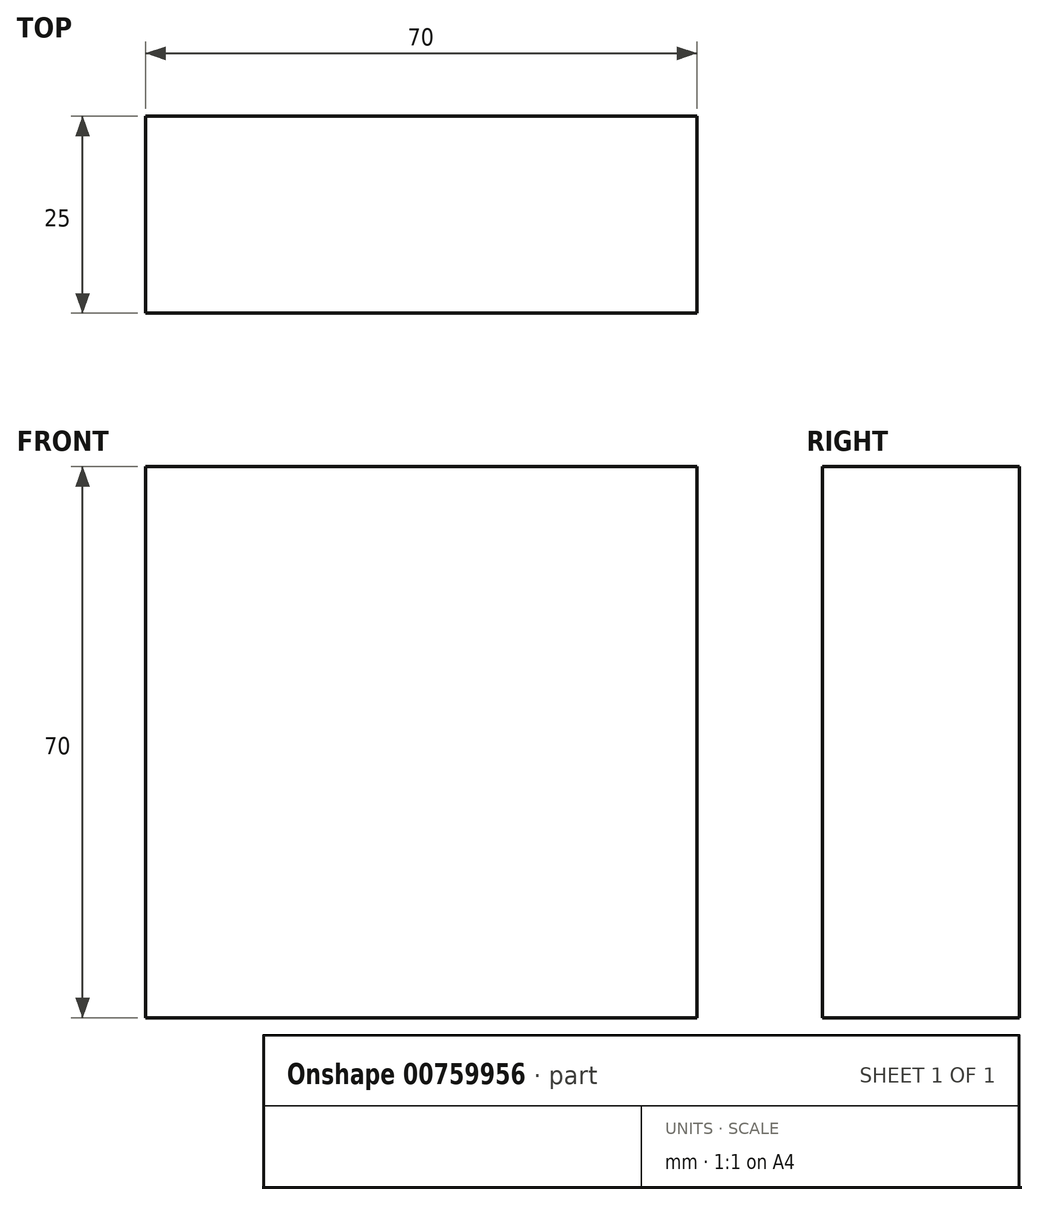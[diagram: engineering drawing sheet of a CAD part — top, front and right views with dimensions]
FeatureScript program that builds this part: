
annotation { "Feature Type Name" : "Feature", "Feature Type Description" : "" }
export const myFeature = defineFeature(function(context is Context, id is Id, definition is map)
    precondition{}
    {
        {
            var Q0;
            Q0=qCreatedBy(makeId("Front.planeOp"),FACE);
            var sketch = newSketch(context, id + "F0", { "sketchPlane" : qUnion([Q0])});
            skLineSegment(sketch, "E0.bottom", {"start": v(-35, 35) * mm, "end": v(35, 35) * mm});
            skLineSegment(sketch, "E0.top", {"start": v(-35, -35) * mm, "end": v(35, -35) * mm});
            skLineSegment(sketch, "E0.left", {"start": v(-35, 35) * mm, "end": v(-35, -35) * mm});
            skLineSegment(sketch, "E0.right", {"start": v(35, 35) * mm, "end": v(35, -35) * mm});
            skPoint(sketch, "E0.middle", {"position": v(0, 0) * mm});
            skSolve(sketch);
        }
        {
            var Q0;
            Q0=makeQuery(id+"F0.imprint","IMPRINT",FACE,{"disambiguationData":[TD([[makeQuery(id+"F0.imprint","IMPRINT",EDGE,{"derivedFrom":sQuery(id+"F0.wireOp",EDGE,"E0.bottom")}),-1.0]])]});
            extrude(context, id + "F1", {"entities" : qUnion([Q0]), "depth" : 25 * mm, "offsetDistance" : 25 * mm});
        }
    });
